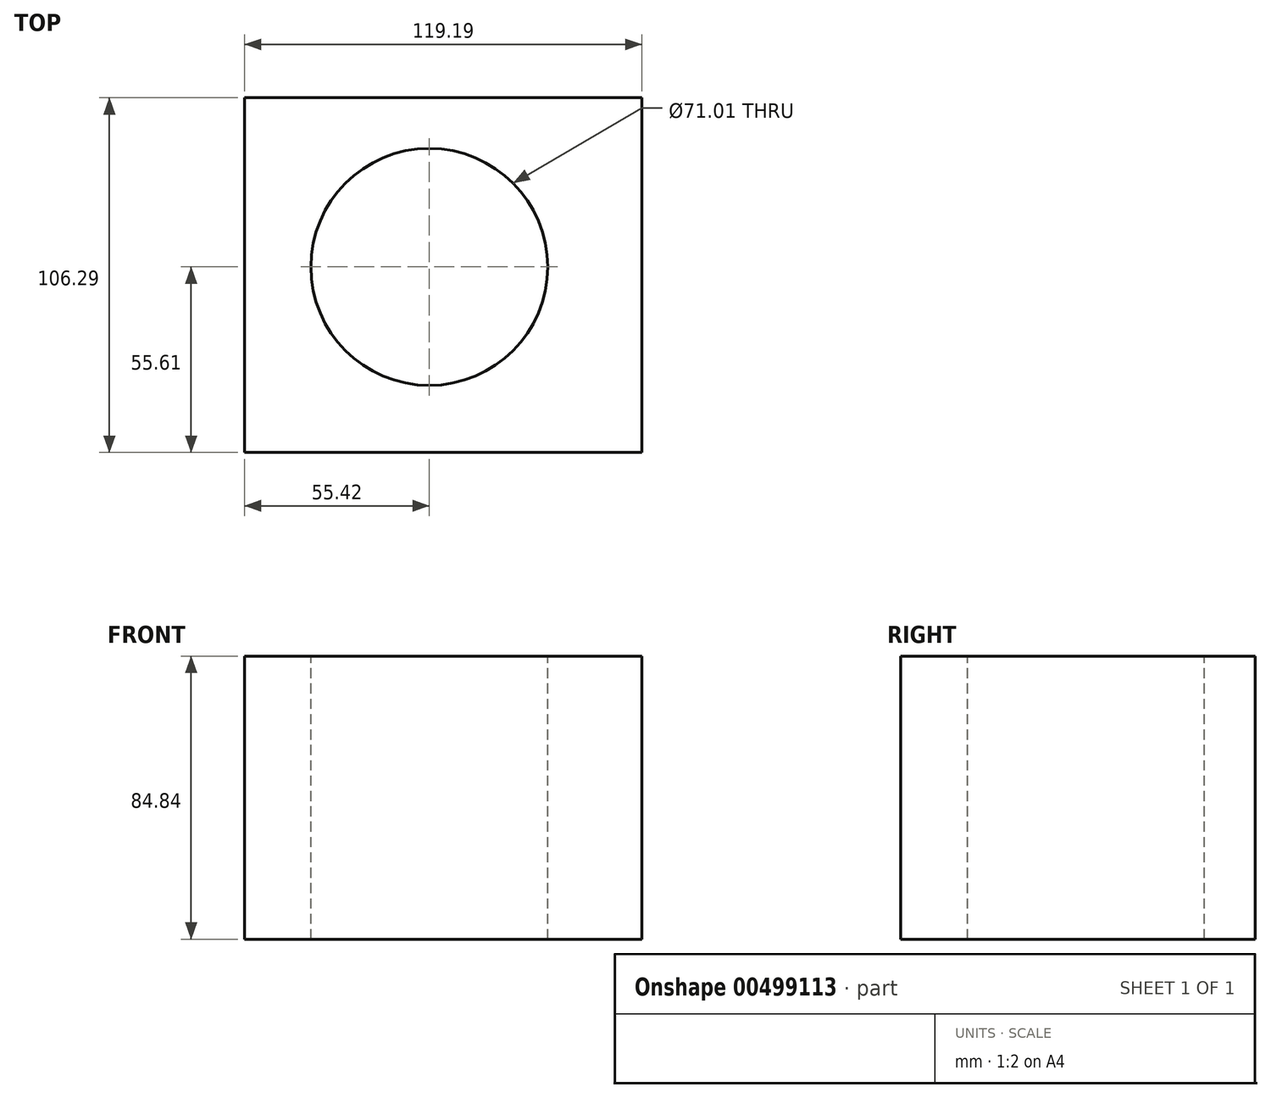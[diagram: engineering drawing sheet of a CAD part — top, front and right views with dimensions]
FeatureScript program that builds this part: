
annotation { "Feature Type Name" : "Feature", "Feature Type Description" : "" }
export const myFeature = defineFeature(function(context is Context, id is Id, definition is map)
    precondition{}
    {
        {
            var Q0;
            Q0=qCreatedBy(makeId("Top.planeOp"),FACE);
            var sketch = newSketch(context, id + "F0", { "sketchPlane" : qUnion([Q0])});
            skLineSegment(sketch, "E0.bottom", {"start": v(-55.42, 50.68) * mm, "end": v(63.77, 50.68) * mm});
            skLineSegment(sketch, "E0.top", {"start": v(-55.42, -55.61) * mm, "end": v(63.77, -55.61) * mm});
            skLineSegment(sketch, "E0.left", {"start": v(-55.42, 50.68) * mm, "end": v(-55.42, -55.61) * mm});
            skLineSegment(sketch, "E0.right", {"start": v(63.77, 50.68) * mm, "end": v(63.77, -55.61) * mm});
            skSolve(sketch);
        }
        {
            var Q0;
            Q0=makeQuery(id+"F0.imprint","IMPRINT",FACE,{"disambiguationData":[TD([[makeQuery(id+"F0.imprint","IMPRINT",EDGE,{"derivedFrom":sQuery(id+"F0.wireOp",EDGE,"E0.bottom")}),-1.0]])]});
            extrude(context, id + "F1", {"entities" : qUnion([Q0]), "endBound" : BoundingType.SYMMETRIC, "depth" : 84.84 * mm});
        }
        {
            var Q0;
            Q0=makeQuery(id+"F1.opExtrude","CAP_FACE",FACE,{"disambiguationData":[OSD([sQuery(id+"F0.wireOp",EDGE,"E0.bottom"),sQuery(id+"F0.wireOp",EDGE,"E0.top"),sQuery(id+"F0.wireOp",EDGE,"E0.left"),sQuery(id+"F0.wireOp",EDGE,"E0.right")])],"isStart":false});
            var sketch = newSketch(context, id + "F2", { "sketchPlane" : qUnion([Q0])});
            skCircle(sketch, "E1", {"center": v(0, 0) * mm, "radius": 35.5 * mm});
            skSolve(sketch);
        }
        {
            var Q0;
            Q0 = qSketchRegion(id + "F2", true);
            extrude(context, id + "F3", {"entities" : qUnion([Q0]), "operationType" : NewBodyOperationType.REMOVE, "oppositeDirection" : true, "depth" : 102.1 * mm});
        }
    });
